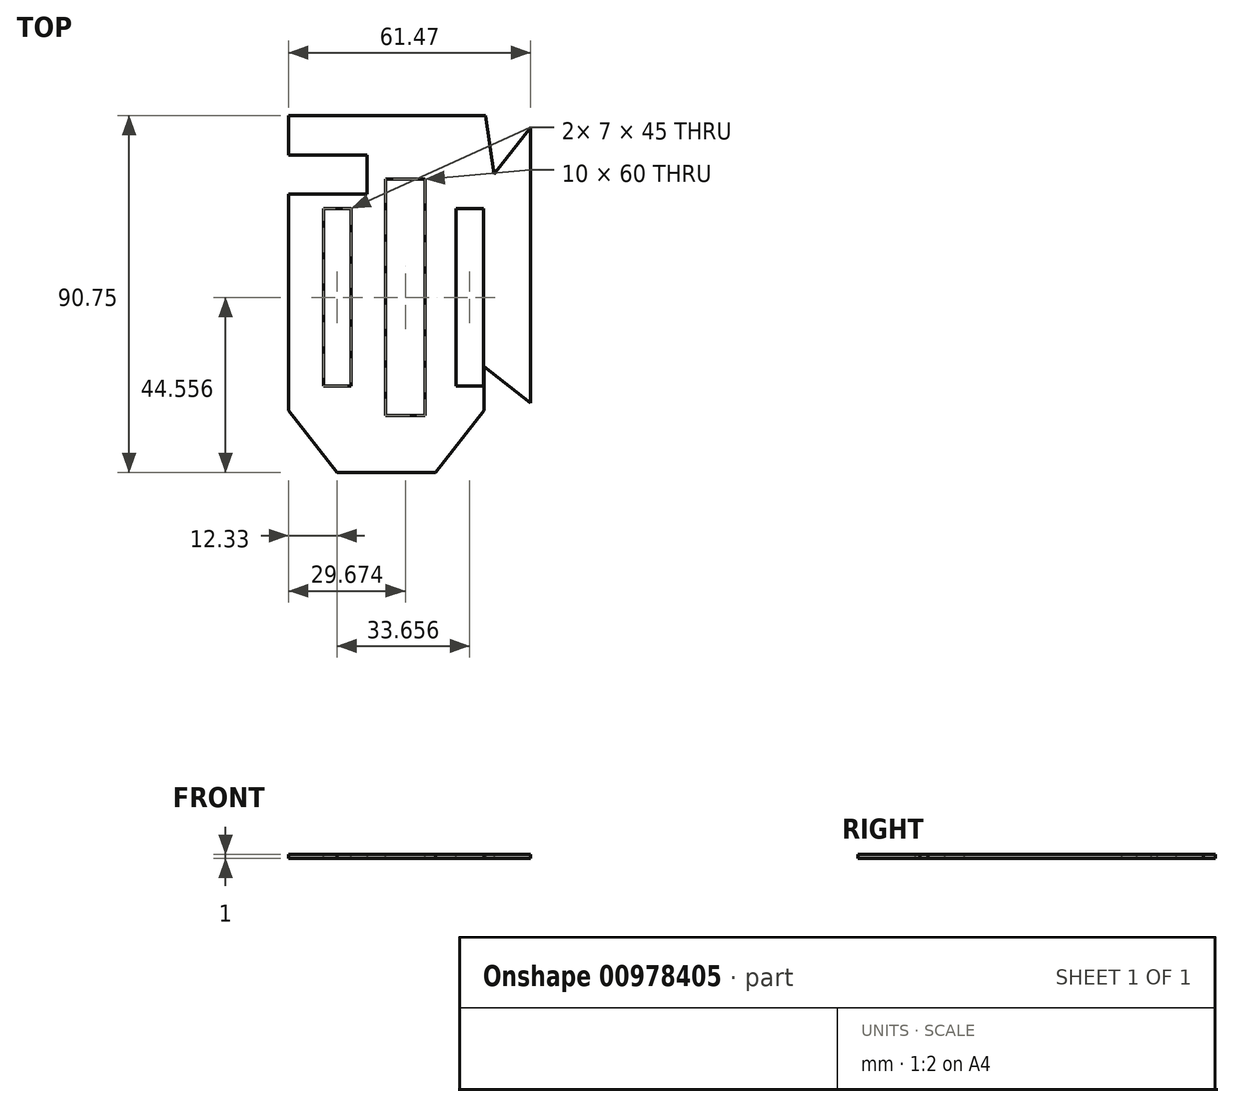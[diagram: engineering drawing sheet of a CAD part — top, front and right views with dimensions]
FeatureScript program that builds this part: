
annotation { "Feature Type Name" : "Feature", "Feature Type Description" : "" }
export const myFeature = defineFeature(function(context is Context, id is Id, definition is map)
    precondition{}
    {
        {
            var Q0;
            Q0=qCreatedBy(makeId("Top.planeOp"),FACE);
            var sketch = newSketch(context, id + "F0", { "sketchPlane" : qUnion([Q0])});
            skLineSegment(sketch, "E0", {"start": v(39.9, 47.4) * mm, "end": v(49.14, 59.2) * mm});
            skLineSegment(sketch, "E1", {"start": v(49.14, 59.2) * mm, "end": v(49.14, -10.8) * mm});
            skLineSegment(sketch, "E2", {"start": v(49.14, -10.8) * mm, "end": v(37.33, -1.55) * mm});
            skLineSegment(sketch, "E3", {"start": v(37.33, -1.55) * mm, "end": v(37.33, -12.77) * mm});
            skLineSegment(sketch, "E4", {"start": v(37.33, -12.77) * mm, "end": v(25, -28.52) * mm});
            skLineSegment(sketch, "E5", {"start": v(25, -28.52) * mm, "end": v(0, -28.52) * mm});
            skLineSegment(sketch, "E6", {"start": v(0, -28.52) * mm, "end": v(-12.33, -12.77) * mm});
            skLineSegment(sketch, "E7", {"start": v(-12.33, -12.77) * mm, "end": v(-12.33, 42.23) * mm});
            skLineSegment(sketch, "E8", {"start": v(-12.33, 42.23) * mm, "end": v(7.67, 42.23) * mm});
            skLineSegment(sketch, "E9", {"start": v(7.67, 42.23) * mm, "end": v(7.67, 52.23) * mm});
            skLineSegment(sketch, "E10", {"start": v(7.67, 52.23) * mm, "end": v(-12.33, 52.23) * mm});
            skLineSegment(sketch, "E11", {"start": v(-12.33, 52.23) * mm, "end": v(-12.33, 62.23) * mm});
            skLineSegment(sketch, "E12", {"start": v(-12.33, 62.23) * mm, "end": v(37.67, 62.23) * mm});
            skLineSegment(sketch, "E13", {"start": v(37.67, 62.23) * mm, "end": v(39.9, 47.4) * mm});
            skSolve(sketch);
        }
        {
            var Q0;
            Q0=makeQuery(id+"F0.imprint","IMPRINT",FACE,{"disambiguationData":[TD([[makeQuery(id+"F0.imprint","IMPRINT",EDGE,{"derivedFrom":sQuery(id+"F0.wireOp",EDGE,"E0")}),-1.0]])]});
            extrude(context, id + "F1", {"entities" : qUnion([Q0]), "depth" : 1 * mm, "offsetDistance" : 25 * mm});
        }
        {
            var Q0;
            Q0=makeQuery(id+"F1.opExtrude","CAP_FACE",FACE,{"disambiguationData":[OSD([sQuery(id+"F0.wireOp",EDGE,"E0"),sQuery(id+"F0.wireOp",EDGE,"E1"),sQuery(id+"F0.wireOp",EDGE,"E2"),sQuery(id+"F0.wireOp",EDGE,"E3"),sQuery(id+"F0.wireOp",EDGE,"E4"),sQuery(id+"F0.wireOp",EDGE,"E5"),sQuery(id+"F0.wireOp",EDGE,"E6"),sQuery(id+"F0.wireOp",EDGE,"E7"),sQuery(id+"F0.wireOp",EDGE,"E8"),sQuery(id+"F0.wireOp",EDGE,"E9"),sQuery(id+"F0.wireOp",EDGE,"E10"),sQuery(id+"F0.wireOp",EDGE,"E11"),sQuery(id+"F0.wireOp",EDGE,"E12"),sQuery(id+"F0.wireOp",EDGE,"E13")])],"isStart":false});
            var sketch = newSketch(context, id + "F2", { "sketchPlane" : qUnion([Q0])});
            skLineSegment(sketch, "E14.bottom", {"start": v(12.34, 46.04) * mm, "end": v(22.34, 46.04) * mm});
            skLineSegment(sketch, "E14.top", {"start": v(12.34, -13.96) * mm, "end": v(22.34, -13.96) * mm});
            skLineSegment(sketch, "E14.left", {"start": v(12.34, 46.04) * mm, "end": v(12.34, -13.96) * mm});
            skLineSegment(sketch, "E14.right", {"start": v(22.34, 46.04) * mm, "end": v(22.34, -13.96) * mm});
            skPoint(sketch, "E14.middle", {"position": v(17.34, 16.04) * mm});
            skLineSegment(sketch, "E15.bottom", {"start": v(-3.5, 38.54) * mm, "end": v(3.5, 38.54) * mm});
            skLineSegment(sketch, "E15.top", {"start": v(-3.5, -6.46) * mm, "end": v(3.5, -6.46) * mm});
            skLineSegment(sketch, "E15.left", {"start": v(-3.5, 38.54) * mm, "end": v(-3.5, -6.46) * mm});
            skLineSegment(sketch, "E15.right", {"start": v(3.5, 38.54) * mm, "end": v(3.5, -6.46) * mm});
            skPoint(sketch, "E15.middle", {"position": v(0, 16.04) * mm});
            skLineSegment(sketch, "E16.bottom", {"start": v(30.16, 38.54) * mm, "end": v(37.16, 38.54) * mm});
            skLineSegment(sketch, "E16.top", {"start": v(30.16, -6.46) * mm, "end": v(37.16, -6.46) * mm});
            skLineSegment(sketch, "E16.left", {"start": v(30.16, 38.54) * mm, "end": v(30.16, -6.46) * mm});
            skLineSegment(sketch, "E16.right", {"start": v(37.16, 38.54) * mm, "end": v(37.16, -6.46) * mm});
            skPoint(sketch, "E16.middle", {"position": v(33.66, 16.04) * mm});
            skSolve(sketch);
        }
        {
            var Q0;
            Q0 = qSketchRegion(id + "F2", true);
            extrude(context, id + "F3", {"entities" : qUnion([Q0]), "operationType" : NewBodyOperationType.REMOVE, "oppositeDirection" : true, "depth" : 25 * mm, "offsetDistance" : 25 * mm});
        }
    });
